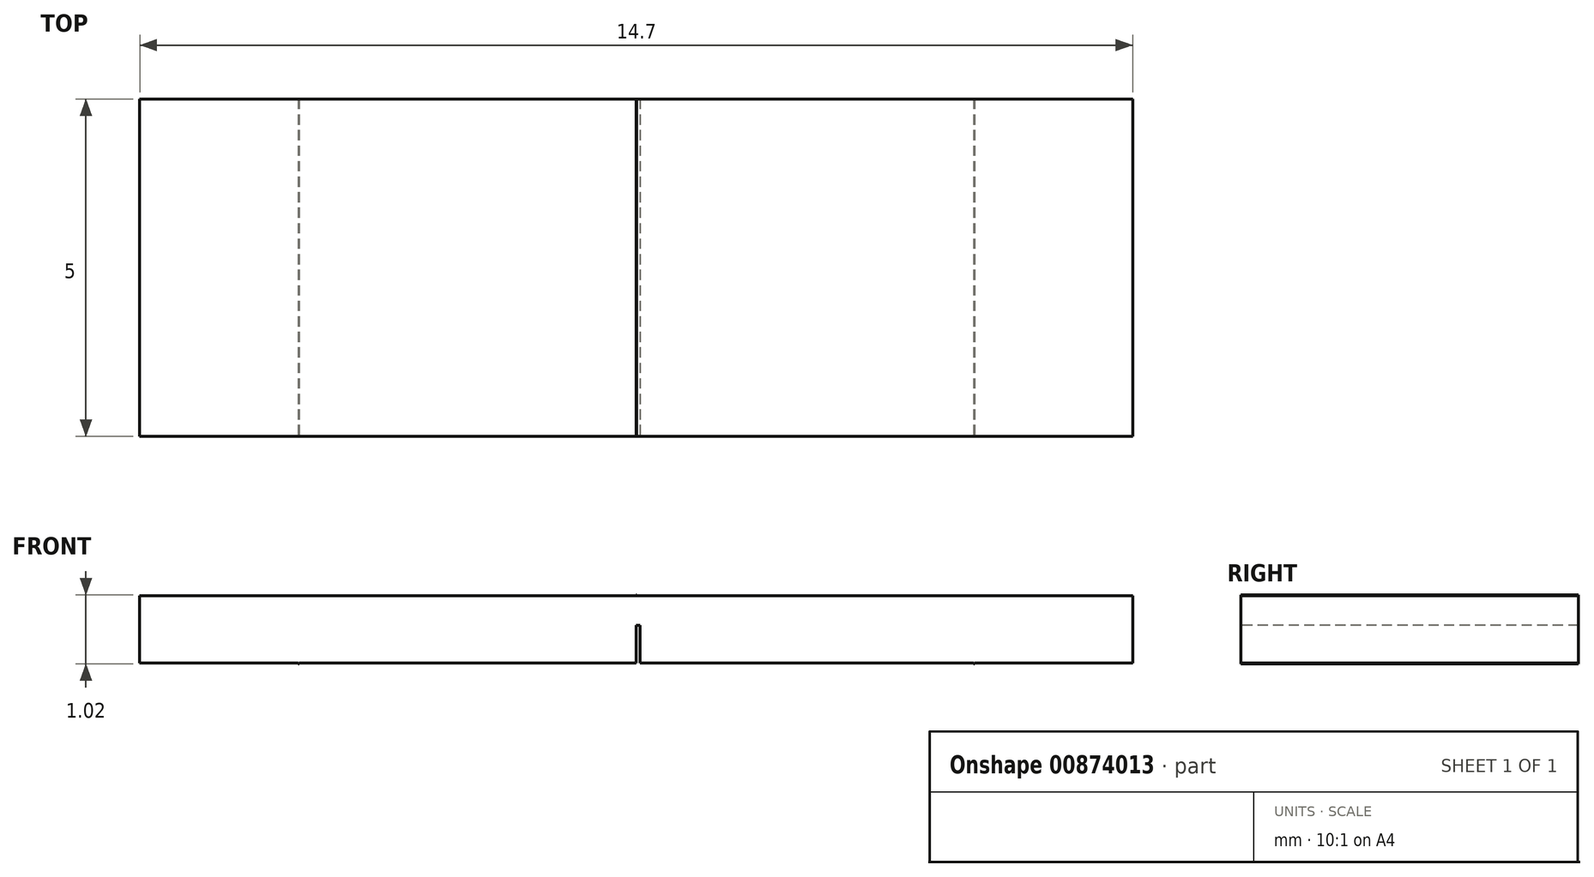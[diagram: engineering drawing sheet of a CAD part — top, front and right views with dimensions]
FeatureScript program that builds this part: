
annotation { "Feature Type Name" : "Feature", "Feature Type Description" : "" }
export const myFeature = defineFeature(function(context is Context, id is Id, definition is map)
    precondition{}
    {
        {
            var Q0;
            Q0=qCreatedBy(makeId("Front.planeOp"),FACE);
            var sketch = newSketch(context, id + "F0", { "sketchPlane" : qUnion([Q0])});
            skLineSegment(sketch, "E0.bottom", {"start": v(7.35, 0.5) * mm, "end": v(-7.35, 0.5) * mm});
            skLineSegment(sketch, "E0.top", {"start": v(7.35, -0.5) * mm, "end": v(-7.35, -0.5) * mm});
            skLineSegment(sketch, "E0.left", {"start": v(7.35, 0.5) * mm, "end": v(7.35, -0.5) * mm});
            skLineSegment(sketch, "E0.right", {"start": v(-7.35, 0.5) * mm, "end": v(-7.35, -0.5) * mm});
            skPoint(sketch, "E0.middle", {"position": v(0, 0) * mm});
            skLineSegment(sketch, "E1", {"start": v(0, 0.5) * mm, "end": v(0, -0.5) * mm});
            skSolve(sketch);
        }
        {
            var Q0;
            Q0 = qSketchRegion(id + "F0", true);
            extrude(context, id + "F1", {"entities" : qUnion([Q0]), "depth" : 5 * mm, "offsetDistance" : 25 * mm});
        }
        {
            var Q0;
            Q0=makeQuery(id+"F1.opExtrude","CAP_FACE",FACE,{"disambiguationData":[OSD([sQuery(id+"F0.wireOp",EDGE,"E0.bottom"),sQuery(id+"F0.wireOp",EDGE,"E0.top"),sQuery(id+"F0.wireOp",EDGE,"E0.left"),sQuery(id+"F0.wireOp",EDGE,"E0.right")])],"isStart":false});
            var sketch = newSketch(context, id + "F2", { "sketchPlane" : qUnion([Q0])});
            skLineSegment(sketch, "E2", {"start": v(0, 0.5) * mm, "end": v(0, -0.5) * mm});
            skLineSegment(sketch, "E3.bottom", {"start": v(0, -0.5) * mm, "end": v(0.05, -0.5) * mm});
            skLineSegment(sketch, "E3.top", {"start": v(0, 0.06) * mm, "end": v(0.05, 0.06) * mm});
            skLineSegment(sketch, "E3.left", {"start": v(0, -0.5) * mm, "end": v(0, 0.06) * mm});
            skLineSegment(sketch, "E3.right", {"start": v(0.05, -0.5) * mm, "end": v(0.05, 0.06) * mm});
            skLineSegment(sketch, "E4.MirrorCS", {"start": v(0, 0.06) * mm, "end": v(-0.05, 0.06) * mm});
            skLineSegment(sketch, "E5.MirrorCS", {"start": v(-0.05, -0.5) * mm, "end": v(-0.05, 0.06) * mm});
            skLineSegment(sketch, "E6.MirrorCS", {"start": v(0, -0.5) * mm, "end": v(-0.05, -0.5) * mm});
            skSolve(sketch);
        }
        {
            var Q0;
            Q0=makeQuery(id+"F2.imprint","IMPRINT",FACE,{"disambiguationData":[TD([[makeQuery(id+"F2.imprint","IMPRINT",EDGE,{"derivedFrom":sQuery(id+"F2.wireOp",EDGE,"E3.left")}),1.0]])]});
            var Q1;
            Q1=makeQuery(id+"F2.imprint","IMPRINT",FACE,{"disambiguationData":[TD([[makeQuery(id+"F2.imprint","IMPRINT",EDGE,{"derivedFrom":sQuery(id+"F2.wireOp",EDGE,"E3.bottom")}),-1.0]])]});
            extrude(context, id + "F3", {"entities" : qUnion([Q0, Q1]), "operationType" : NewBodyOperationType.REMOVE, "endBound" : BoundingType.THROUGH_ALL, "oppositeDirection" : true, "depth" : 25 * mm, "offsetDistance" : 25 * mm});
        }
        {
            var Q0;
            Q0=makeQuery(id+"F1.opExtrude","SWEPT_FACE",FACE,{"disambiguationData":[OSD([sQuery(id+"F0.wireOp",EDGE,"E0.bottom")])]});
            var sketch = newSketch(context, id + "F4", { "sketchPlane" : qUnion([Q0])});
            skLineSegment(sketch, "E7", {"start": v(0, -5) * mm, "end": v(0, 0) * mm});
            skLineSegment(sketch, "E8.bottom", {"start": v(0, -5) * mm, "end": v(0, -5) * mm});
            skLineSegment(sketch, "E8.top", {"start": v(0, 0) * mm, "end": v(0, 0) * mm});
            skPoint(sketch, "E8.middle", {"position": v(0, -2.5) * mm});
            skSolve(sketch);
        }
        {
            var Q0;
            Q0 = qSketchRegion(id + "F4", true);
            extrude(context, id + "F5", {"entities" : qUnion([Q0]), "operationType" : NewBodyOperationType.ADD, "depth" : 0.01 * mm, "offsetDistance" : 25 * mm});
        }
        {
            var Q0;
            {var subQ0=sQuery(id+"F0.wireOp",EDGE,"E0.right");var subQ2=sQuery(id+"F0.wireOp",EDGE,"E0.top");Q0=makeQuery(id+"F3.boolean.opBoolean","SPLIT",FACE,{"disambiguationData":[TD([makeQuery(id+"F1.opExtrude","SWEPT_FACE",FACE,{"disambiguationData":[OSD([subQ0])]})])],"derivedFrom":makeQuery(id+"F1.opExtrude","SWEPT_FACE",FACE,{"disambiguationData":[OSD([subQ2])]})});}
            var sketch = newSketch(context, id + "F6", { "sketchPlane" : qUnion([Q0])});
            skLineSegment(sketch, "E9", {"start": v(0, 5) * mm, "end": v(0, 0) * mm});
            skLineSegment(sketch, "E10", {"start": v(0, 0) * mm, "end": v(5, 0) * mm});
            skLineSegment(sketch, "E11", {"start": v(5, 0) * mm, "end": v(5, 5) * mm});
            skLineSegment(sketch, "E12", {"start": v(5, 5) * mm, "end": v(-5, 5) * mm});
            skLineSegment(sketch, "E13", {"start": v(-5, 5) * mm, "end": v(-5, 0) * mm});
            skLineSegment(sketch, "E14.bottom", {"start": v(-5, 0) * mm, "end": v(-5, 0) * mm});
            skLineSegment(sketch, "E14.top", {"start": v(-5, 5) * mm, "end": v(-5, 5) * mm});
            skLineSegment(sketch, "E14.left", {"start": v(-5, 0) * mm, "end": v(-5, 5) * mm});
            skLineSegment(sketch, "E14.right", {"start": v(-5, 0) * mm, "end": v(-5, 5) * mm});
            skPoint(sketch, "E14.middle", {"position": v(-5, 2.5) * mm});
            skLineSegment(sketch, "E15.bottom", {"start": v(5, 0) * mm, "end": v(5, 0) * mm});
            skLineSegment(sketch, "E15.top", {"start": v(5, 5) * mm, "end": v(5, 5) * mm});
            skPoint(sketch, "E15.middle", {"position": v(5, 2.5) * mm});
            skSolve(sketch);
        }
        {
            var Q0;
            {var subQ0=sQuery(id+"F6.wireOp",EDGE,"E13");Q0=makeQuery(id+"F6.imprint","IMPRINT",FACE,{"disambiguationData":[TD([[makeQuery(id+"F6.imprint","IMPRINT",EDGE,{"derivedFrom":subQ0}),1.0]])]});}
            var Q1;
            {var subQ0=sQuery(id+"F6.wireOp",EDGE,"E13");Q1=makeQuery(id+"F6.imprint","IMPRINT",FACE,{"disambiguationData":[TD([[makeQuery(id+"F6.imprint","IMPRINT",EDGE,{"derivedFrom":subQ0}),-1.0]])]});}
            var Q2;
            {var subQ0=sQuery(id+"F6.wireOp",EDGE,"E11");Q2=makeQuery(id+"F6.imprint","IMPRINT",FACE,{"disambiguationData":[TD([[makeQuery(id+"F6.imprint","IMPRINT",EDGE,{"derivedFrom":subQ0}),-1.0]])]});}
            var Q3;
            {var subQ0=sQuery(id+"F6.wireOp",EDGE,"E11");Q3=makeQuery(id+"F6.imprint","IMPRINT",FACE,{"disambiguationData":[TD([[makeQuery(id+"F6.imprint","IMPRINT",EDGE,{"derivedFrom":subQ0}),1.0]])]});}
            extrude(context, id + "F7", {"entities" : qUnion([Q0, Q1, Q2, Q3]), "operationType" : NewBodyOperationType.ADD, "depth" : 0.01 * mm, "offsetDistance" : 25 * mm});
        }
    });
